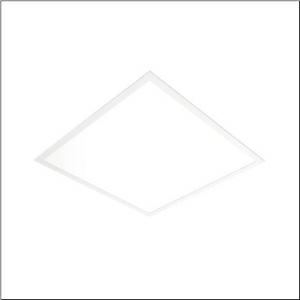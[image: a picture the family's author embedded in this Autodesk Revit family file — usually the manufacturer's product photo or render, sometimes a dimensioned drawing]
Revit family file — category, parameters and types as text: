
# Revit family: apollon_r__41_51mh12h72443_9ce2
name_source: partatom
category: Lighting Fixtures
units: mm (PartAtom-declared; Revit-internal decimal feet)

## family parameters
Cut with Voids When Loaded = No
Host = Face
Light Source = No
Part Type = Normal
Room Calculation Point = No
Round Connector Dimension = Use Diameter
Shared = No

## types (1)
- Apollon® 41 (1 x LED, 5000 lm, 38.5 W, 4000K)
    Apparent Load = 39 VA
    CIE Flux Codes = 61 87 97 100 100
    Color Rendering = 80
    Color Temperature = 4000K
    Default Elevation = 1800 mm
    Description = Apollon® 41, office luminaire, primary optical cover: prismatic diffuser, of PS, light emission: direct distribution, primary light characteristic: symmetric, installation type: lay-in mounting, LED, rated luminous flux: 5.000lm, luminous efficacy: 130lm/W, light colour: 840, colour temperature: 4000K, control gear: ON/OFF, with terminal, 3-pole, mains connection: 220..240V, AC, 50/60Hz, rated input power: 38.5W, housing, of aluminium section, traffic white (RAL 9016), module: M600, length: 595mm, width: 595mm, height: 60mm, recess depth: 180mm, housing upper side, of sheet steel, protection rating (complete): IP20, protection rating (lamp compartment, on room side): IP40, insulation class (complete): insulation class II (safety insulation), certification: CE, ENEC, impact resistance: IK03, permissible operating ambient temperature: -25..+40°C, packaging unit: 1 piece
    Height = 0 mm  [stored 0 ft]
    Lamp = 1 x LED
    Lamp Light Flux = 5000 lm
    Lamp Power = 38.5 W
    Lamp count = 1
    Length = 600 mm
    Luminous efficacy = 130 lm/W
    Manufacturer = Siteco
    ModVariant = No
    Model = 51MH12H72443
    Mounting Place = Ceiling
    Mounting Type = Recessed
    Number of Poles = 1
    OnlyDefault = Yes
    Power Factor = 1
    Product Name = Apollon® 41
    Product group = office luminaire | ceiling recessed
    ProductGroupID = 400
    Protection Class = Protection class II
    Protection Degree = IP 20
    RLX_Detail_Level = 1
    RLX_Emergency_Light_Flux = 0 lm
    RLX_Emergency_Type = 0
    RLX_Emergency_Type_DB = No
    RlxData = <blob elided: 12293 chars, md5=728eee0b>
    Socket = socket
    Standby Power = 0 W
    System Light Flux = 5000 lm
    System Power = 39 W
    Type Comments = Product without accessories
    Type Image = l_1291024.jpg
    URL = http://relux.com
    VarID = ---
    Voltage = 0 V
    Weight = 0.00 kg
    Width = 600 mm

note: [stored X ft] marks values corroborated as IEEE doubles in the binary element streams (Revit-internal decimal feet)

## geometry (parser evidence)
native form markers: Sweep x9
no freeform markers — native parametric forms only
